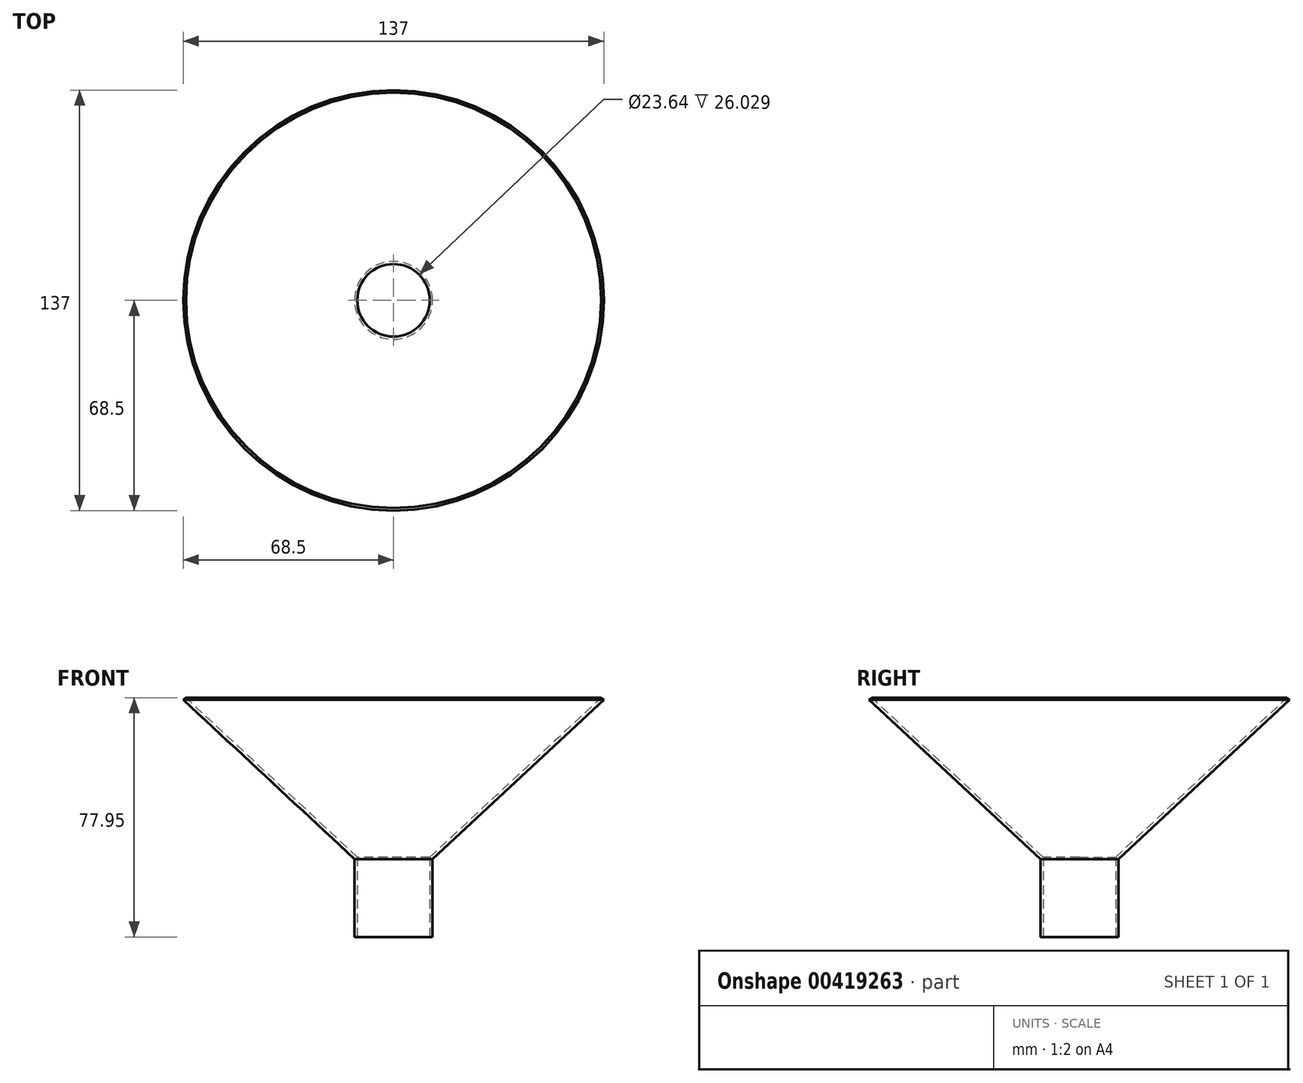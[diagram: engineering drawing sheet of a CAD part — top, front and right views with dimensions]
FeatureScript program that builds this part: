
annotation { "Feature Type Name" : "Feature", "Feature Type Description" : "" }
export const myFeature = defineFeature(function(context is Context, id is Id, definition is map)
    precondition{}
    {
        {
            var Q0;
            Q0=qCreatedBy(makeId("Front.planeOp"),FACE);
            var sketch = newSketch(context, id + "F0", { "sketchPlane" : qUnion([Q0])});
            skLineSegment(sketch, "E0", {"start": v(0, 0) * mm, "end": v(55.8, 51.89) * mm});
            skLineSegment(sketch, "E1", {"start": v(0, 0) * mm, "end": v(0, -25.4) * mm});
            skLineSegment(sketch, "E2", {"start": v(0, -25.4) * mm, "end": v(-12.7, -25.4) * mm});
            skLineSegment(sketch, "E3", {"start": v(-12.7, -25.4) * mm, "end": v(-12.7, 0) * mm});
            skLineSegment(sketch, "E4", {"start": v(-12.7, 0) * mm, "end": v(-1.56, 0) * mm});
            skLineSegment(sketch, "E5", {"start": v(-1.56, 0) * mm, "end": v(54.96, 52.55) * mm});
            skLineSegment(sketch, "E6", {"start": v(54.96, 52.55) * mm, "end": v(55.8, 51.89) * mm});
            skSolve(sketch);
        }
        {
            var Q0;
            Q0=makeQuery(id+"F0.imprint","IMPRINT",FACE,{"disambiguationData":[TD([[makeQuery(id+"F0.imprint","IMPRINT",EDGE,{"derivedFrom":sQuery(id+"F0.wireOp",EDGE,"E0")}),1.0]])]});
            var Q1;
            Q1=sQuery(id+"F0.wireOp",EDGE,"E3");
            revolve(context, id + "F1", {"entities" : qUnion([Q0]), "axis" : qUnion([Q1]), "revolveType" : RevolveType.FULL});
        }
        {
            var Q0;
            Q0=makeQuery(id+"F1.opRevolve","SWEPT_FACE",FACE,{"disambiguationData":[OSD([sQuery(id+"F0.wireOp",EDGE,"E2")])]});
            var sketch = newSketch(context, id + "F2", { "sketchPlane" : qUnion([Q0])});
            skCircle(sketch, "E7", {"center": v(-12.7, 0) * mm, "radius": 11.82 * mm});
            skSolve(sketch);
        }
        {
            var Q0;
            Q0=makeQuery(id+"F2.imprint","IMPRINT",FACE,{"disambiguationData":[TD([[makeQuery(id+"F2.imprint","IMPRINT",EDGE,{"derivedFrom":sQuery(id+"F2.wireOp",EDGE,"E7")}),1.0]])]});
            var sketch = newSketch(context, id + "F3", { "sketchPlane" : qUnion([Q0])});
            skSolve(sketch);
        }
        {
            var Q0;
            Q0 = qSketchRegion(id + "F3", true);
            var Q1;
            Q1=makeQuery(id+"F2.imprint","IMPRINT",FACE,{"disambiguationData":[TD([[makeQuery(id+"F2.imprint","IMPRINT",EDGE,{"derivedFrom":sQuery(id+"F2.wireOp",EDGE,"E7")}),1.0]])]});
            extrude(context, id + "F4", {"entities" : qUnion([Q0, Q1]), "operationType" : NewBodyOperationType.REMOVE, "oppositeDirection" : true, "depth" : 50.8 * mm});
        }
    });
